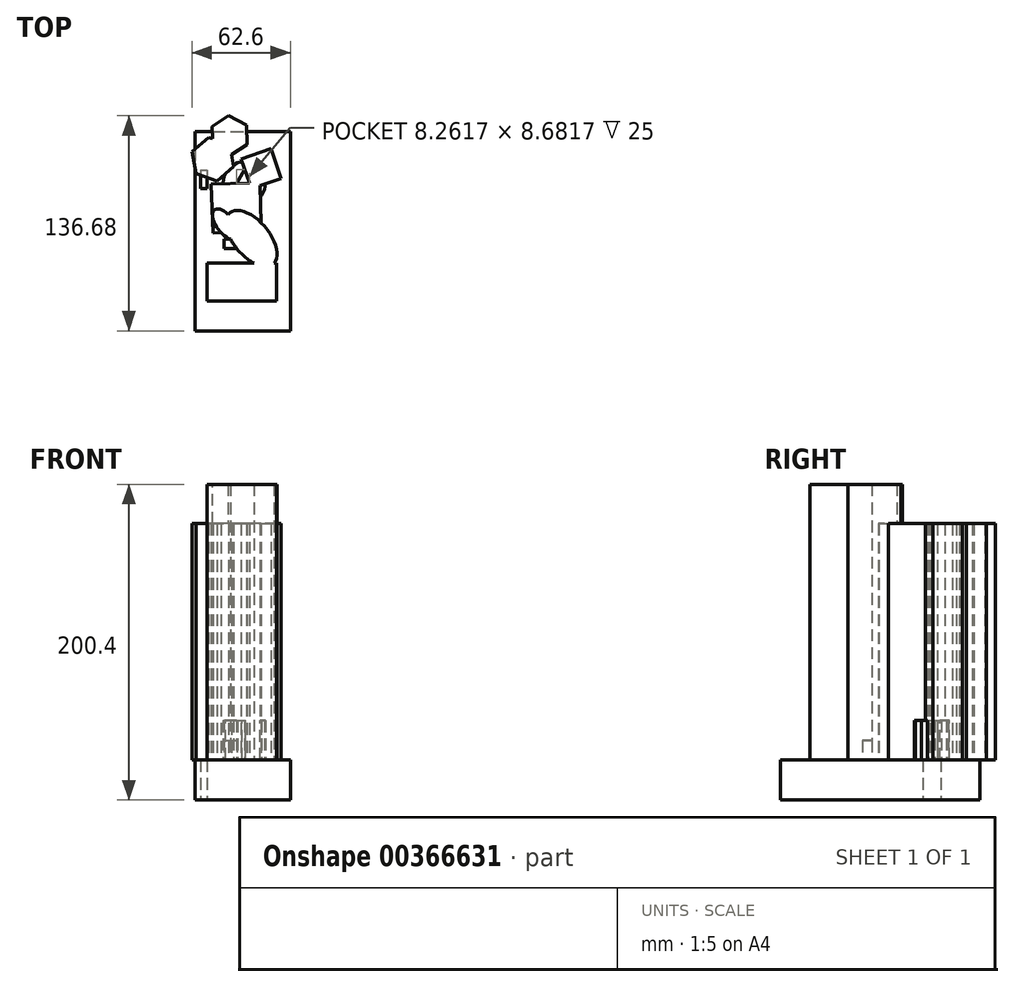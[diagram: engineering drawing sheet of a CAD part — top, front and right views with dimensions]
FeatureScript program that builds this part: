
annotation { "Feature Type Name" : "Feature", "Feature Type Description" : "" }
export const myFeature = defineFeature(function(context is Context, id is Id, definition is map)
    precondition{}
    {
        {
            var Q0;
            Q0=qCreatedBy(makeId("Top.planeOp"),FACE);
            var sketch = newSketch(context, id + "F0", { "sketchPlane" : qUnion([Q0])});
            skLineSegment(sketch, "E0.bottom", {"start": v(-22.76, 38.72) * mm, "end": v(-18.5, 38.72) * mm});
            skLineSegment(sketch, "E0.top", {"start": v(-22.76, 27.08) * mm, "end": v(-18.5, 27.08) * mm});
            skLineSegment(sketch, "E0.left", {"start": v(-22.76, 38.72) * mm, "end": v(-22.76, 27.08) * mm});
            skLineSegment(sketch, "E0.right", {"start": v(-18.5, 38.72) * mm, "end": v(-18.5, 27.08) * mm});
            skPoint(sketch, "E0.middle", {"position": v(-20.64, 32.9) * mm});
            skLineSegment(sketch, "E1.bottom", {"start": v(-26.08, 63.29) * mm, "end": v(34.34, 63.29) * mm});
            skLineSegment(sketch, "E1.top", {"start": v(-26.08, -63.29) * mm, "end": v(34.34, -63.29) * mm});
            skLineSegment(sketch, "E1.left", {"start": v(-26.08, 63.29) * mm, "end": v(-26.08, -63.29) * mm});
            skLineSegment(sketch, "E1.right", {"start": v(34.34, 63.29) * mm, "end": v(34.34, -63.29) * mm});
            skPoint(sketch, "E1.middle", {"position": v(4.13, 0) * mm});
            skSolve(sketch);
        }
        {
            var Q0;
            Q0 = qSketchRegion(id + "F0", true);
            extrude(context, id + "F1", {"entities" : qUnion([Q0]), "endBound" : BoundingType.SYMMETRIC, "depth" : 25.4 * mm});
        }
        {
            var Q0;
            Q0=makeQuery(id+"F1.opExtrude","CAP_FACE",FACE,{"disambiguationData":[OSD([sQuery(id+"F0.wireOp",EDGE,"E0.bottom"),sQuery(id+"F0.wireOp",EDGE,"E0.top"),sQuery(id+"F0.wireOp",EDGE,"E0.left"),sQuery(id+"F0.wireOp",EDGE,"E0.right"),sQuery(id+"F0.wireOp",EDGE,"E1.bottom"),sQuery(id+"F0.wireOp",EDGE,"E1.top"),sQuery(id+"F0.wireOp",EDGE,"E1.left"),sQuery(id+"F0.wireOp",EDGE,"E1.right")])],"isStart":false});
            var sketch = newSketch(context, id + "F2", { "sketchPlane" : qUnion([Q0])});
            skArc(sketch, "E2", {"start": v(23, 36.98) * mm, "mid": v(5.76, 60.74) * mm, "end": v(-10.92, 36.6) * mm});
            skSolve(sketch);
        }
        {
            var Q0;
            {var subQ7=sQuery(id+"F0.wireOp",EDGE,"E0.bottom");Q0=makeQuery(id+"F2.imprint","IMPRINT",FACE,{"disambiguationData":[TD([[makeQuery(id+"F2.imprint","IMPRINT",EDGE,{"derivedFrom":makeQuery(id+"F1.opExtrude","CAP_EDGE",EDGE,{"disambiguationData":[OSD([subQ7])],"isStart":false})}),1.0]])]});}
            var sketch = newSketch(context, id + "F3", { "sketchPlane" : qUnion([Q0])});
            skCircle(sketch, "E3.cCircle", {"center": v(5.1, 30.6) * mm, "radius": 3.89 * mm, "construction": true});
            skLineSegment(sketch, "E3.0", {"start": v(1.43, 31.89) * mm, "end": v(2.01, 32.96) * mm});
            skLineSegment(sketch, "E3.1", {"start": v(2.01, 32.96) * mm, "end": v(2.9, 33.8) * mm});
            skLineSegment(sketch, "E3.2", {"start": v(2.9, 33.8) * mm, "end": v(4, 34.32) * mm});
            skLineSegment(sketch, "E3.3", {"start": v(4, 34.32) * mm, "end": v(5.2, 34.48) * mm});
            skLineSegment(sketch, "E3.4", {"start": v(5.2, 34.48) * mm, "end": v(6.4, 34.26) * mm});
            skLineSegment(sketch, "E3.5", {"start": v(6.4, 34.26) * mm, "end": v(7.46, 33.68) * mm});
            skLineSegment(sketch, "E3.6", {"start": v(7.46, 33.68) * mm, "end": v(8.3, 32.8) * mm});
            skLineSegment(sketch, "E3.7", {"start": v(8.3, 32.8) * mm, "end": v(8.82, 31.7) * mm});
            skLineSegment(sketch, "E3.8", {"start": v(8.82, 31.7) * mm, "end": v(8.98, 30.5) * mm});
            skLineSegment(sketch, "E3.9", {"start": v(8.98, 30.5) * mm, "end": v(8.76, 29.3) * mm});
            skLineSegment(sketch, "E3.10", {"start": v(8.76, 29.3) * mm, "end": v(8.18, 28.23) * mm});
            skLineSegment(sketch, "E3.11", {"start": v(8.18, 28.23) * mm, "end": v(7.3, 27.4) * mm});
            skLineSegment(sketch, "E3.12", {"start": v(7.3, 27.4) * mm, "end": v(6.2, 26.87) * mm});
            skLineSegment(sketch, "E3.13", {"start": v(6.2, 26.87) * mm, "end": v(5, 26.7) * mm});
            skLineSegment(sketch, "E3.14", {"start": v(5, 26.7) * mm, "end": v(3.8, 26.93) * mm});
            skLineSegment(sketch, "E3.15", {"start": v(3.8, 26.93) * mm, "end": v(2.73, 27.5) * mm});
            skLineSegment(sketch, "E3.16", {"start": v(2.73, 27.5) * mm, "end": v(1.9, 28.4) * mm});
            skLineSegment(sketch, "E3.17", {"start": v(1.9, 28.4) * mm, "end": v(1.37, 29.49) * mm});
            skLineSegment(sketch, "E3.18", {"start": v(1.37, 29.49) * mm, "end": v(1.21, 30.7) * mm});
            skLineSegment(sketch, "E3.19", {"start": v(1.21, 30.7) * mm, "end": v(1.43, 31.89) * mm});
            skCircle(sketch, "E4.cCircle", {"center": v(5.1, 30.6) * mm, "radius": 13.54 * mm, "construction": true});
            skLineSegment(sketch, "E4.0", {"start": v(5.1, 44.13) * mm, "end": v(9.28, 43.47) * mm});
            skLineSegment(sketch, "E4.1", {"start": v(9.28, 43.47) * mm, "end": v(13.05, 41.55) * mm});
            skLineSegment(sketch, "E4.2", {"start": v(13.05, 41.55) * mm, "end": v(16.05, 38.55) * mm});
            skLineSegment(sketch, "E4.3", {"start": v(16.05, 38.55) * mm, "end": v(17.97, 34.78) * mm});
            skLineSegment(sketch, "E4.4", {"start": v(17.97, 34.78) * mm, "end": v(18.63, 30.6) * mm});
            skLineSegment(sketch, "E4.5", {"start": v(18.63, 30.6) * mm, "end": v(17.97, 26.41) * mm});
            skLineSegment(sketch, "E4.6", {"start": v(17.97, 26.41) * mm, "end": v(16.05, 22.64) * mm});
            skLineSegment(sketch, "E4.7", {"start": v(16.05, 22.64) * mm, "end": v(13.05, 19.64) * mm});
            skLineSegment(sketch, "E4.8", {"start": v(13.05, 19.64) * mm, "end": v(9.28, 17.72) * mm});
            skLineSegment(sketch, "E4.9", {"start": v(9.28, 17.72) * mm, "end": v(5.1, 17.06) * mm});
            skLineSegment(sketch, "E4.10", {"start": v(5.1, 17.06) * mm, "end": v(0.91, 17.72) * mm});
            skLineSegment(sketch, "E4.11", {"start": v(0.91, 17.72) * mm, "end": v(-2.86, 19.64) * mm});
            skLineSegment(sketch, "E4.12", {"start": v(-2.86, 19.64) * mm, "end": v(-5.85, 22.64) * mm});
            skLineSegment(sketch, "E4.13", {"start": v(-5.85, 22.64) * mm, "end": v(-7.78, 26.41) * mm});
            skLineSegment(sketch, "E4.14", {"start": v(-7.78, 26.41) * mm, "end": v(-8.44, 30.6) * mm});
            skLineSegment(sketch, "E4.15", {"start": v(-8.44, 30.6) * mm, "end": v(-7.78, 34.78) * mm});
            skLineSegment(sketch, "E4.16", {"start": v(-7.78, 34.78) * mm, "end": v(-5.85, 38.55) * mm});
            skLineSegment(sketch, "E4.17", {"start": v(-5.85, 38.55) * mm, "end": v(-2.86, 41.55) * mm});
            skLineSegment(sketch, "E4.18", {"start": v(-2.86, 41.55) * mm, "end": v(0.91, 43.47) * mm});
            skLineSegment(sketch, "E4.19", {"start": v(0.91, 43.47) * mm, "end": v(5.1, 44.13) * mm});
            skCircle(sketch, "E5.cCircle", {"center": v(5.1, 30.6) * mm, "radius": 8.43 * mm, "construction": true});
            skLineSegment(sketch, "E5.0", {"start": v(5.2, 39.02) * mm, "end": v(12.35, 26.3) * mm});
            skLineSegment(sketch, "E5.1", {"start": v(12.35, 26.3) * mm, "end": v(-2.25, 26.47) * mm});
            skLineSegment(sketch, "E5.2", {"start": v(-2.25, 26.47) * mm, "end": v(5.2, 39.02) * mm});
            skSolve(sketch);
        }
        {
            var Q0;
            Q0 = qSketchRegion(id + "F3", true);
            extrude(context, id + "F4", {"entities" : qUnion([Q0]), "operationType" : NewBodyOperationType.ADD, "depth" : 25 * mm});
        }
        {
            var Q0;
            Q0=makeQuery(id+"F2.imprint","IMPRINT",FACE,{"disambiguationData":[TD([[makeQuery(id+"F2.imprint","IMPRINT",EDGE,{"derivedFrom":makeQuery(id+"F1.opExtrude","CAP_EDGE",EDGE,{"disambiguationData":[OSD([sQuery(id+"F0.wireOp",EDGE,"E0.bottom")])],"isStart":false})}),1.0]])]});
            var sketch = newSketch(context, id + "F5", { "sketchPlane" : qUnion([Q0])});
            skLineSegment(sketch, "E6.bottom", {"start": v(-18.59, -20.31) * mm, "end": v(25.48, -20.31) * mm});
            skLineSegment(sketch, "E6.top", {"start": v(-18.59, -44.45) * mm, "end": v(25.48, -44.45) * mm});
            skLineSegment(sketch, "E6.left", {"start": v(-18.59, -20.31) * mm, "end": v(-18.59, -44.45) * mm});
            skLineSegment(sketch, "E6.right", {"start": v(25.48, -20.31) * mm, "end": v(25.48, -44.45) * mm});
            skPoint(sketch, "E6.middle", {"position": v(3.45, -32.38) * mm});
            skSolve(sketch);
        }
        {
            var Q0;
            Q0 = qSketchRegion(id + "F5", true);
            extrude(context, id + "F6", {"entities" : qUnion([Q0]), "operationType" : NewBodyOperationType.ADD, "depth" : 25 * mm});
        }
        {
            var Q0;
            Q0=qCreatedBy(makeId("Top.planeOp"),FACE);
            var sketch = newSketch(context, id + "F7", { "sketchPlane" : qUnion([Q0])});
            skLineSegment(sketch, "E7.bottom", {"start": v(-7.86, -11.11) * mm, "end": v(20.12, -11.11) * mm});
            skLineSegment(sketch, "E7.top", {"start": v(-7.86, -4.98) * mm, "end": v(20.12, -4.98) * mm});
            skLineSegment(sketch, "E7.left", {"start": v(-7.86, -11.11) * mm, "end": v(-7.86, -4.98) * mm});
            skLineSegment(sketch, "E7.right", {"start": v(20.12, -11.11) * mm, "end": v(20.12, -4.98) * mm});
            skSolve(sketch);
        }
        {
            var Q0;
            Q0 = qSketchRegion(id + "F7", true);
            extrude(context, id + "F8", {"entities" : qUnion([Q0]), "operationType" : NewBodyOperationType.ADD, "depth" : 25 * mm});
        }
        {
            var Q0;
            Q0=makeQuery(id+"F2.imprint","IMPRINT",FACE,{"disambiguationData":[TD([[makeQuery(id+"F2.imprint","IMPRINT",EDGE,{"derivedFrom":makeQuery(id+"F1.opExtrude","CAP_EDGE",EDGE,{"disambiguationData":[OSD([sQuery(id+"F0.wireOp",EDGE,"E0.bottom")])],"isStart":false})}),1.0]])]});
            var sketch = newSketch(context, id + "F9", { "sketchPlane" : qUnion([Q0])});
            skEllipse(sketch, "E8", {"center": v(-6.9, 4.4) * mm, "majorRadius": 11.61 * mm, "minorRadius": 5.57 * mm, "majorAxis": v(0.61, -0.8)});
            skEllipse(sketch, "E9", {"center": v(9.58, -4.6) * mm, "majorRadius": 11.29 * mm, "minorRadius": 21.34 * mm, "majorAxis": v(0.76, 0.65)});
            skSolve(sketch);
        }
        {
            var Q0;
            Q0 = qSketchRegion(id + "F9", true);
            extrude(context, id + "F10", {"entities" : qUnion([Q0]), "operationType" : NewBodyOperationType.ADD, "depth" : 25 * mm});
        }
        {
            var Q0;
            Q0=makeQuery(id+"F2.imprint","IMPRINT",FACE,{"disambiguationData":[TD([[makeQuery(id+"F2.imprint","IMPRINT",EDGE,{"derivedFrom":makeQuery(id+"F1.opExtrude","CAP_EDGE",EDGE,{"disambiguationData":[OSD([sQuery(id+"F0.wireOp",EDGE,"E0.bottom")])],"isStart":false})}),1.0]])]});
            var sketch = newSketch(context, id + "F11", { "sketchPlane" : qUnion([Q0])});
            skEllipse(sketch, "E10", {"center": v(-11.88, -15.71) * mm, "majorRadius": 26.22 * mm, "minorRadius": 11.86 * mm, "majorAxis": v(0.45, 0.9)});
            skSolve(sketch);
        }
        {
            var Q0;
            Q0=makeQuery(id+"F11.imprint","IMPRINT",FACE,{"disambiguationData":[TD([[makeQuery(id+"F11.imprint","IMPRINT",EDGE,{"derivedFrom":makeQuery(id+"F2.imprint","IMPRINT",EDGE,{"derivedFrom":makeQuery(id+"F1.opExtrude","CAP_EDGE",EDGE,{"disambiguationData":[OSD([sQuery(id+"F0.wireOp",EDGE,"E0.bottom")])],"isStart":false})})}),1.0]])]});
            var sketch = newSketch(context, id + "F12", { "sketchPlane" : qUnion([Q0])});
            skCircle(sketch, "E11.cCircle", {"center": v(-14.96, 45.76) * mm, "radius": 14.1 * mm, "construction": true});
            skLineSegment(sketch, "E11.0", {"start": v(-4.27, 54.95) * mm, "end": v(-1.65, 41.1) * mm});
            skLineSegment(sketch, "E11.1", {"start": v(-1.65, 41.1) * mm, "end": v(-12.34, 31.9) * mm});
            skLineSegment(sketch, "E11.2", {"start": v(-12.34, 31.9) * mm, "end": v(-25.65, 36.57) * mm});
            skLineSegment(sketch, "E11.3", {"start": v(-25.65, 36.57) * mm, "end": v(-28.26, 50.43) * mm});
            skLineSegment(sketch, "E11.4", {"start": v(-28.26, 50.43) * mm, "end": v(-17.57, 59.62) * mm});
            skLineSegment(sketch, "E11.5", {"start": v(-17.57, 59.62) * mm, "end": v(-4.27, 54.95) * mm});
            skCircle(sketch, "E12.cCircle", {"center": v(-4.27, 60.78) * mm, "radius": 12.62 * mm, "construction": true});
            skLineSegment(sketch, "E12.0", {"start": v(6.93, 54.95) * mm, "end": v(-3.72, 48.17) * mm});
            skLineSegment(sketch, "E12.1", {"start": v(-3.72, 48.17) * mm, "end": v(-14.91, 54) * mm});
            skLineSegment(sketch, "E12.2", {"start": v(-14.91, 54) * mm, "end": v(-15.46, 66.61) * mm});
            skLineSegment(sketch, "E12.3", {"start": v(-15.46, 66.61) * mm, "end": v(-4.82, 73.4) * mm});
            skLineSegment(sketch, "E12.4", {"start": v(-4.82, 73.4) * mm, "end": v(6.38, 67.56) * mm});
            skLineSegment(sketch, "E12.5", {"start": v(6.38, 67.56) * mm, "end": v(6.93, 54.95) * mm});
            skCircle(sketch, "E13.cCircle", {"center": v(15.73, 39.73) * mm, "radius": 14.1 * mm, "construction": true});
            skLineSegment(sketch, "E13.0", {"start": v(21.94, 52.4) * mm, "end": v(28.4, 33.52) * mm});
            skLineSegment(sketch, "E13.1", {"start": v(28.4, 33.52) * mm, "end": v(9.52, 27.06) * mm});
            skLineSegment(sketch, "E13.2", {"start": v(9.52, 27.06) * mm, "end": v(3.07, 45.94) * mm});
            skLineSegment(sketch, "E13.3", {"start": v(3.07, 45.94) * mm, "end": v(21.94, 52.4) * mm});
            skCircle(sketch, "E14.cCircle", {"center": v(0, 14.9) * mm, "radius": 21.81 * mm, "construction": true});
            skLineSegment(sketch, "E14.0", {"start": v(15.93, 0) * mm, "end": v(-14.9, -1.02) * mm});
            skLineSegment(sketch, "E14.1", {"start": v(-14.9, -1.02) * mm, "end": v(-15.93, 29.81) * mm});
            skLineSegment(sketch, "E14.2", {"start": v(-15.93, 29.81) * mm, "end": v(14.9, 30.83) * mm});
            skLineSegment(sketch, "E14.3", {"start": v(14.9, 30.83) * mm, "end": v(15.93, 0) * mm});
            skSolve(sketch);
        }
        {
            var Q0;
            Q0 = qSketchRegion(id + "F12", true);
            var Q1;
            Q1=makeQuery(id+"F10.boolean.opBoolean","MERGE",FACE,{"derivedFrom":[makeQuery(id+"F6.opExtrude","CAP_FACE",FACE,{"disambiguationData":[OSD([sQuery(id+"F5.wireOp",EDGE,"E6.bottom"),sQuery(id+"F5.wireOp",EDGE,"E6.top"),sQuery(id+"F5.wireOp",EDGE,"E6.left"),sQuery(id+"F5.wireOp",EDGE,"E6.right")])],"isStart":false}),makeQuery(id+"F10.opExtrude","CAP_FACE",FACE,{"disambiguationData":[OSD([sQuery(id+"F9.wireOp",EDGE,"E8"),sQuery(id+"F9.wireOp",EDGE,"E9")])],"isStart":false})]});
            extrude(context, id + "F13", {"entities" : qUnion([Q0, Q1]), "operationType" : NewBodyOperationType.ADD, "depth" : 150 * mm, "offsetDistance" : 25 * mm});
        }
    });
